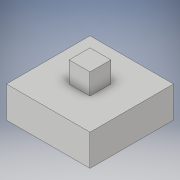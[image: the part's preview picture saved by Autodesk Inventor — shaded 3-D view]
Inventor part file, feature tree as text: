
AUTODESK INVENTOR PART (.ipt)
format: ipt  version: 2019 (Build 230136000, 136)  size: 98,816 bytes
history: native  units: in
note: dims shown in document units (in); Inventor stores cm internally (conversion verified against a paired STEP export)
features: extrude x2, sketch x2
ambient origin geometry x8: Origin, YZ Plane, XZ Plane, XY Plane, X Axis, Y Axis, Z Axis, Center Point
bodies: Solid1 (feature_tree)
feature tree (4):
  extrude  "Extrusion1"  Depth=0.315in
  extrude  "Extrusion2"  Depth=0.0787in
  sketch  "Sketch1"  dims[d0=0.315in d1=0.315in]
  sketch  "Sketch2"  dims[d2=0.1181in d3=0.0in d4=0.0787in d5=0.0787in d6=0.0787in d7=0.0in]
